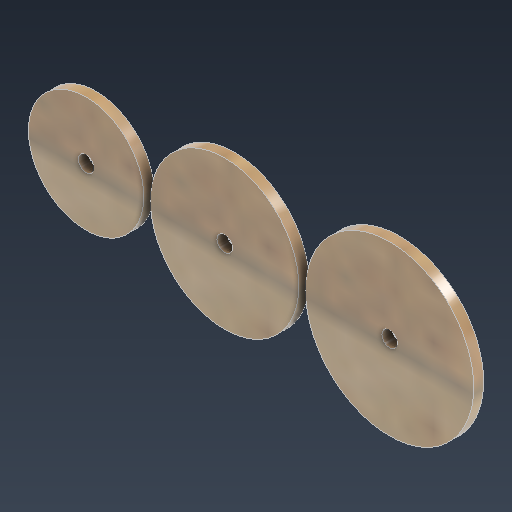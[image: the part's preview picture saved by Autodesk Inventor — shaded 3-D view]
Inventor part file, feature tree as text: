
AUTODESK INVENTOR PART (.ipt)
format: ipt  version: 2025.3 (Build 293356000, 356)  size: 256,512 bytes
history: native  units: mm
features: other x3, extrude x3, sketch x1
ambient origin geometry x8: Origin, YZ Plane, XZ Plane, XY Plane, X Axis, Y Axis, Z Axis, Center Point
bodies: Body1 (feature_tree), Body2 (feature_tree), Body3 (feature_tree)
feature tree (7):
  other  "35mm wheel"
  sketch  "草圖1"
  extrude  "擠出1"  Depth=35.0mm
  extrude  "擠出2"  Depth=45.0mm
  extrude  "擠出3"  Depth=51.0mm
  other  "40mm wheel"
  other  "45mm wheel"
